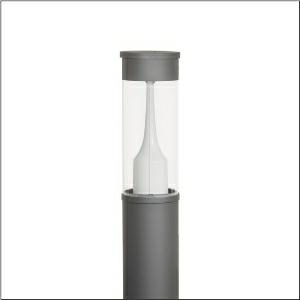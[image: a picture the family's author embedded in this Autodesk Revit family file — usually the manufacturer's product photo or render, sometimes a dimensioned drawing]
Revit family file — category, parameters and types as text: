
# Revit family: city-light_260_iq___st1_2a_5xa5295kf14h_47e0
name_source: partatom
category: Lighting Fixtures
units: mm (PartAtom-declared; Revit-internal decimal feet)

## family parameters
Cut with Voids When Loaded = No
Host = Face
Light Source = No
Part Type = Normal
Room Calculation Point = No
Round Connector Dimension = Use Diameter
Shared = No

## types (1)
- --- (1 x LED, 1540 lm, 10 W, 4000K)
    Apparent Load = 10 VA
    CIE Flux Codes = 22 61 93 96 100
    Color Rendering = 70
    Color Temperature = 4000K
    Default Elevation = 1800 mm
    Description = City-Light 260 iQ, light pillar, Module 540 iQ-SR, primary light control with 3 zone facetted reflector, of plastic, silver coated, highly specular, structured, primary optical cover: cover, of PMMA, transparent, partly coated, light distribution: ST1.2a, primary light characteristic: asymmetric, LED, High Power LED, rated luminous flux: 1.540lm, luminous efficacy: 154lm/W, light colour: 740, colour temperature: 4000K, control gear: ECG iQ, control: presetting dimming logarithmic, Street-Remote, Auto-Match, Temp-Guard, Lumen-Switch, Night-Set, Smart-Wire, Light-Fading, Desk-Remote (wireless, voltage-free reading and setting of iQ features in the workshop via application-optimized NFC function/RFID function), optimised constant luminous flux control (CLO 2.0), with terminal, 6-pole, max. 2.5mm², mains connection: 220..240V, AC, 50/60Hz, start of lifetime: 10W, end of lifetime: 10W, reduction: 5W, luminaire housing, cylindrical, of extruded aluminium section, coated, Siteco® metallic grey (DB 702S), length: 2.600mm, diameter: 200mm, Module 540 iQ-SR, traffic white (RAL 9016), equipment: standard, protection rating (complete): IP65, insulation class (complete): insulation class II (safety insulation), certification: CE, ENEC, VDE, packaging unit: 1 piece

Light Distribution: ST1.2a
    Height = 500 mm
    Lamp = 1 x LED
    Lamp Light Flux = 1540 lm
    Lamp Power = 10 W
    Lamp count = 1
    Length = 200 mm  [stored 0.656168 ft]
    Luminous efficacy = 154 lm/W
    Manufacturer = Siteco
    ModVariant = No
    Model = 5XA5295KF14H
    Number of Poles = 1
    OnlyDefault = Yes
    Power Factor = 1
    Product Name = City-Light 260 iQ | ST1.2a
    Product group = light pillar | pylon top
    ProductGroupID = 6103
    Protection Class = Protection class II
    Protection Degree = IP 65
    RLX_Detail_Level = 1
    RlxData = <blob elided: 64805 chars, md5=c86f89e2>
    Socket = socket
    Standby Power = 0 W
    System Light Flux = 1540 lm
    System Power = 10 W
    Type Comments = factory setting: luminous flux: 100 % | dim-lin: 254 | 401 mA
    Type Image = l_1006918.jpg
    URL = http://relux.com
    VarID = @adj_070417
    Voltage = 0 V
    Weight = 0.00 kg
    Width = 0 mm  [stored 0 ft]

note: [stored X ft] marks values corroborated as IEEE doubles in the binary element streams (Revit-internal decimal feet)

## geometry (parser evidence)
native form markers: Blend x4, Sweep x9
no freeform markers — native parametric forms only
